# Revit family: shelf 140_430
name_source: partatom
category: Furniture
units: mm (PartAtom-declared; Revit-internal decimal feet)

## family parameters
Always vertical = Yes
Cut with Voids When Loaded = No
OmniClass Number = 23.31.25.00
Room Calculation Point = No
Shared = Yes
Work Plane-Based = No

## types (6) — shared parameters
BASENUMBER = Shelf 140/430
BIMOBJECT = Sanitary: Accessories
CATALOG = Hansgrohe
DESIGN = Germany
ETIM = EC011163 | Shelf
GTINCODE = 4059625458464
IFC = Furnishing element
MASTERFORMAT = 10 28 00 | Toilet, Bath, and Laundry Accessories
Manufacturer = Hansgrohe
NAME = Xelu Q Shelf 140/430
NBSYN = $BASENUMBER.-$ARTNR.--$SURFACE.-$LODLEVEL.
NN = Shelf 140/430
OBJECTTYPE = Object (single object)
OMNICLASS = 23-31 25 00 | Toilet and Bath Specialties
PERMALINK = 54144XXX
PRODUCTFAMILY = Xelu Q
PRODUCTGROUP = Shelfs
PRODUCTURL = https://pro.hansgrohe.com
REGIONSET = Worldwide
SPECIFICATION = Surfaces:    - 54144000 Chrome  - 54144670 Matt Black  - 54144700 Matt White      Specification:    null
UNIFORMATII = E2010 | Fixed Furnishings
UNSPSC = 301815 | Sanitary ware
WEIGHT = 0
etim7_EC011163 = EC011163

## per-type parameters (varying)
| type | ARTNR | LINA | LODLEVEL | Model | NB | SURFACE |
| Shelf 140_430-54144000--CHROME-200 | 54144000 | Shelf 140/430-54144000--CHROME-200 | 200 | Shelf 140/430-54144000--CHROME-200 | Shelf 140/430-54144000--CHROME-200 | CHROME |
| Shelf 140_430-54144000--CHROME-400 | 54144000 | Shelf 140/430-54144000--CHROME-400 | 400 | Shelf 140/430-54144000--CHROME-400 | Shelf 140/430-54144000--CHROME-400 | CHROME |
| Shelf 140_430-54144670--MATT_BLACK-200 | 54144670 | Shelf 140/430-54144670--MATT_BLACK-200 | 200 | Shelf 140/430-54144670--MATT_BLACK-200 | Shelf 140/430-54144670--MATT_BLACK-200 | MATT_BLACK |
| Shelf 140_430-54144670--MATT_BLACK-400 | 54144670 | Shelf 140/430-54144670--MATT_BLACK-400 | 400 | Shelf 140/430-54144670--MATT_BLACK-400 | Shelf 140/430-54144670--MATT_BLACK-400 | MATT_BLACK |
| Shelf 140_430-54144700--MATT_WHITE-200 | 54144700 | Shelf 140/430-54144700--MATT_WHITE-200 | 200 | Shelf 140/430-54144700--MATT_WHITE-200 | Shelf 140/430-54144700--MATT_WHITE-200 | MATT_WHITE |
| Shelf 140_430-54144700--MATT_WHITE-400 | 54144700 | Shelf 140/430-54144700--MATT_WHITE-400 | 400 | Shelf 140/430-54144700--MATT_WHITE-400 | Shelf 140/430-54144700--MATT_WHITE-400 | MATT_WHITE |

type visibility flags: 6 boolean params named "<type name>_RX0RY0RZ0TX0TY0TZ0_V" — each type sets only its own to Yes (folded from table)

## geometry (parser evidence)
native form markers: Sweep x25
no freeform markers — native parametric forms only
